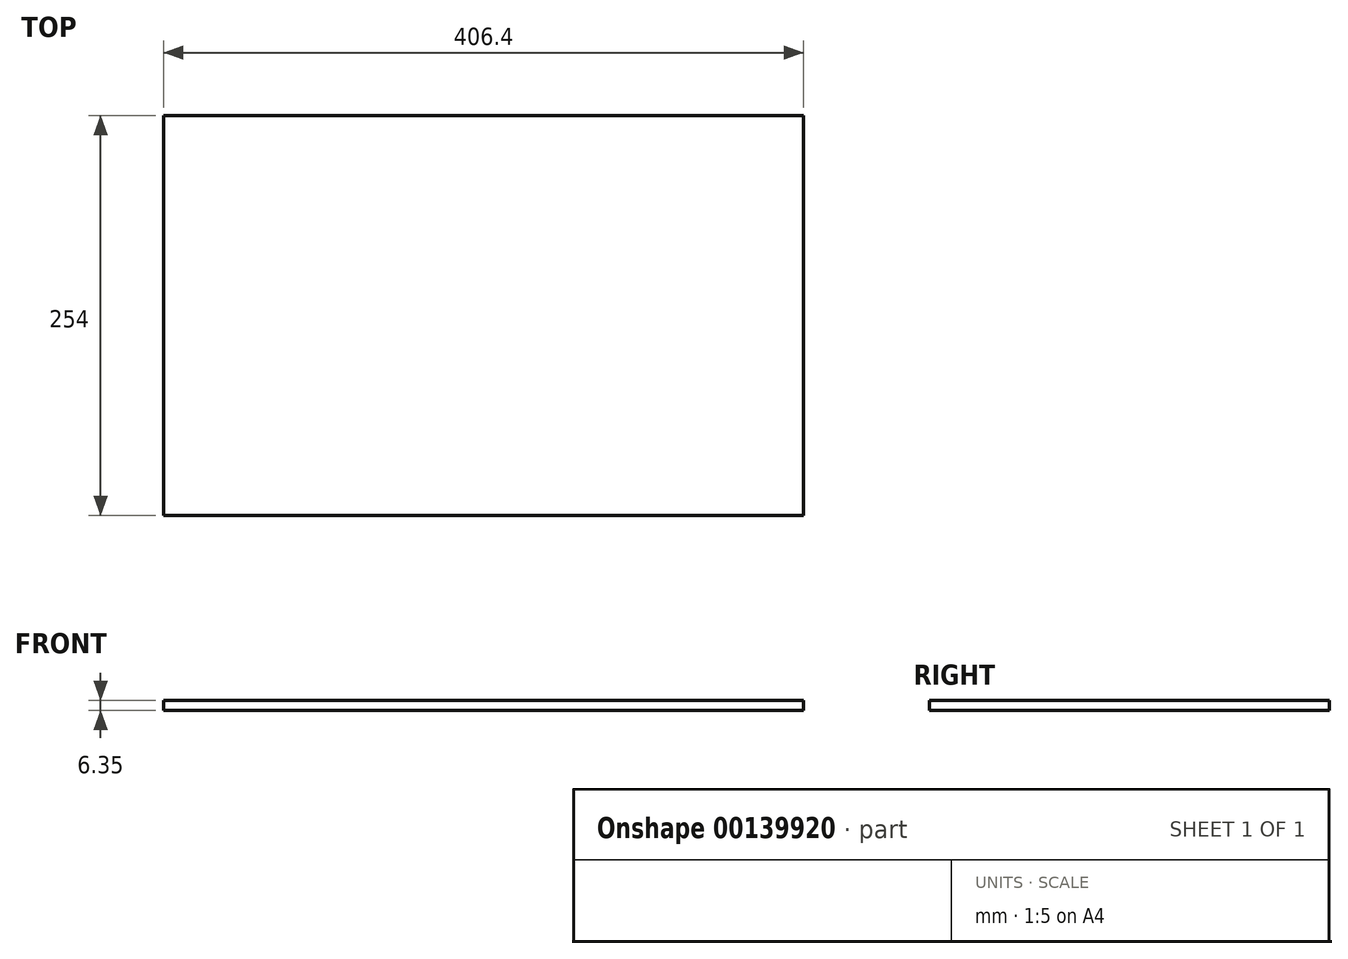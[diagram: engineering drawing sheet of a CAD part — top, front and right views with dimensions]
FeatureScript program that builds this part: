
annotation { "Feature Type Name" : "Feature", "Feature Type Description" : "" }
export const myFeature = defineFeature(function(context is Context, id is Id, definition is map)
    precondition{}
    {
        {
            var Q0;
            Q0=qCreatedBy(makeId("Top.planeOp"),FACE);
            var sketch = newSketch(context, id + "F0", { "sketchPlane" : qUnion([Q0])});
            skLineSegment(sketch, "E0.bottom", {"start": v(-177.62, 138.67) * mm, "end": v(228.78, 138.67) * mm});
            skLineSegment(sketch, "E0.top", {"start": v(-177.62, -115.33) * mm, "end": v(228.78, -115.33) * mm});
            skLineSegment(sketch, "E0.left", {"start": v(-177.62, 138.67) * mm, "end": v(-177.62, -115.33) * mm});
            skLineSegment(sketch, "E0.right", {"start": v(228.78, 138.67) * mm, "end": v(228.78, -115.33) * mm});
            skSolve(sketch);
        }
        {
            var Q0;
            Q0=makeQuery(id+"F0.imprint","IMPRINT",FACE,{"disambiguationData":[TD([[makeQuery(id+"F0.imprint","IMPRINT",EDGE,{"derivedFrom":sQuery(id+"F0.wireOp",EDGE,"E0.bottom")}),-1.0]])]});
            extrude(context, id + "F1", {"entities" : qUnion([Q0]), "depth" : 6.35 * mm});
        }
    });
